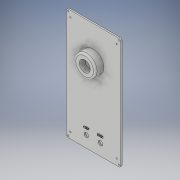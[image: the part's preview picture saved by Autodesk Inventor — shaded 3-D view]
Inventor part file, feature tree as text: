
AUTODESK INVENTOR PART (.ipt)
format: ipt  version: 2019 (Build 230136000, 136)  size: 333,312 bytes
history: native  units: in
note: dims shown in document units (in); Inventor stores cm internally (conversion verified against a paired STEP export)
features: sketch x6, extrude x3, hole x3, other x2, fillet x1, imported_body x1
ambient origin geometry x8: Origin, YZ Plane, XZ Plane, XY Plane, X Axis, Y Axis, Z Axis, Center Point
bodies: Solid1 (feature_tree)
feature tree (16):
  other  "InnerDoorCover"
  extrude  "Extrusion1"  Depth=7.87in
  hole  "ScrewHoles"  [1 undecoded]
  hole  "InputHoles"  [1 undecoded]
  extrude  "ButtonStand"  Depth=0.13in
  hole  "ButtonHole"  [1 undecoded]
  fillet  "Fillet1"  Radius=0.13in
  other  "Text"
  extrude  "ButtonSink"  Depth=0.3in
  imported_body  "Base"
  sketch  "Sketch2"  dims[d0=3.83in d1=7.87in]
  sketch  "Sketch3"  dims[d2=0.125in d3=0.1in d4=0.0in]
  sketch  "Sketch4"  dims[d5=0.13in d6=0.13in]
  sketch  "Sketch5"  dims[d7=0.13in d8=0.13in]
  sketch  "Sketch6"  dims[d9=0.13in d10=0.13in d11=0.13in]
  sketch  "Sketch7"  dims[d12=0.13in d13=0.43in d14=0.28in d15=0.28in d16=0.43in d17=0.43in d18=0.28in d19=0.43in d20=0.28in d21=0.1in d22=0.75in d23=0.375in d24=0.25in d25=0.5635in d26=0.1in d27=0.8108in d30=0.315in d31=0.75in d32=0.375in d33=0.25in d34=0.5635in d35=0.1in d36=0.8108in d37=1.5in d38=0.6in d39=0.0in d40=0.78in d41=0.75in d42=0.375in d43=0.25in d44=0.5635in d45=0.1in d46=0.8108in d47=0.125in d48=0.05in d49=0.0in d50=1.1in d51=0.3in d52=0.0in d28=0.75in d29=0.8108in]
note: 3 required parameter values undecoded (feature->parameter linkage not recoverable at this tier; creation-order binding heuristic only, values carry confidence <= 0.55)
